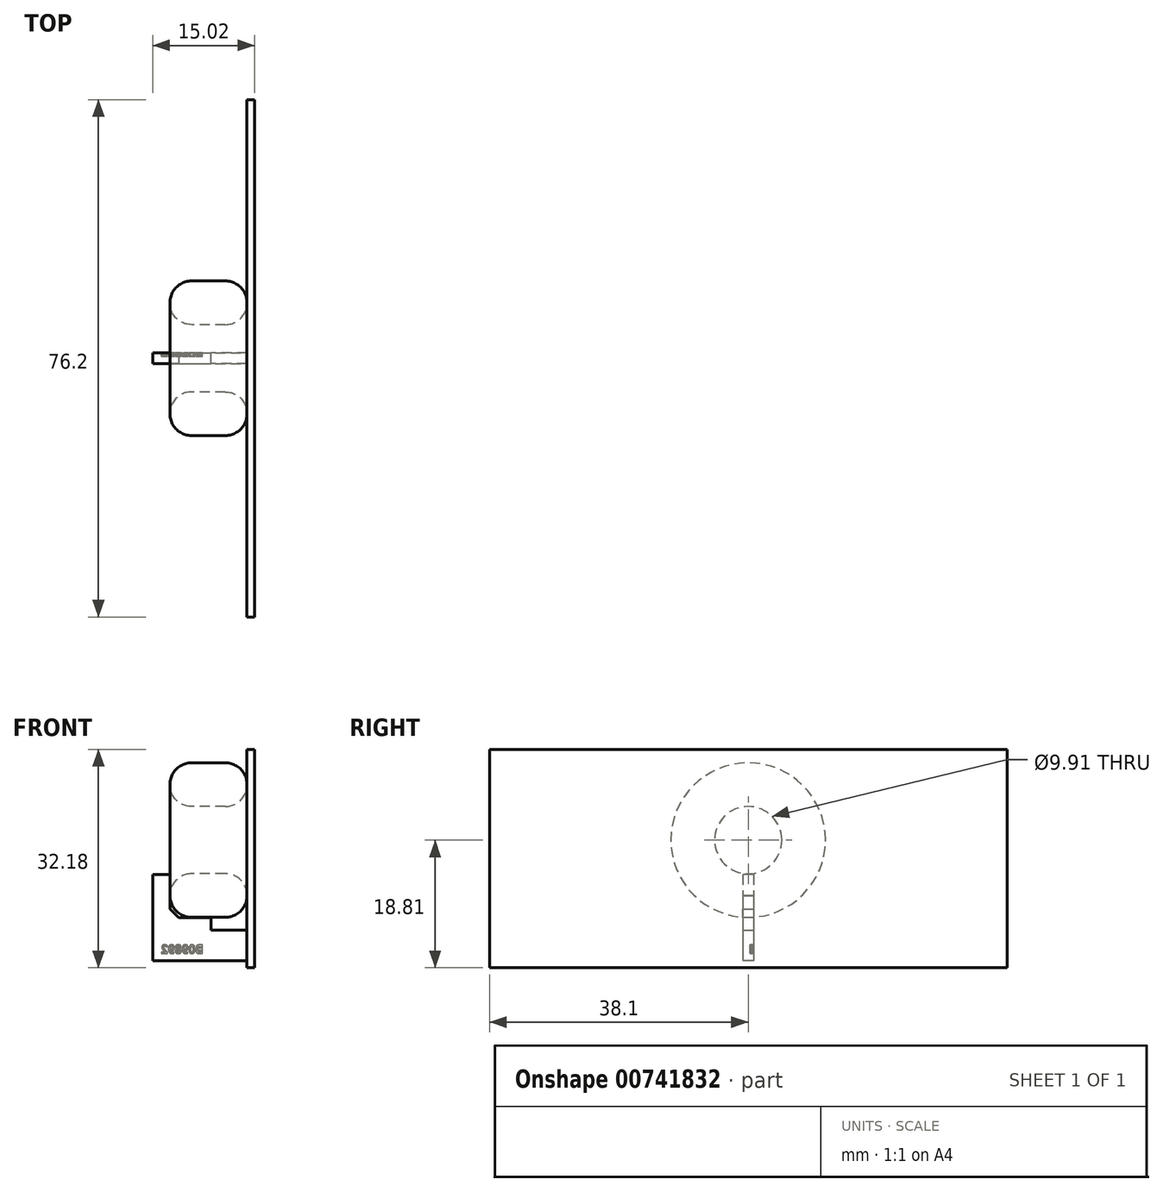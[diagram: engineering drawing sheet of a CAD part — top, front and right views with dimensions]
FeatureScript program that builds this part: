
annotation { "Feature Type Name" : "Feature", "Feature Type Description" : "" }
export const myFeature = defineFeature(function(context is Context, id is Id, definition is map)
    precondition{}
    {
        {
            var Q0;
            Q0=qCreatedBy(makeId("Front.planeOp"),FACE);
            var sketch = newSketch(context, id + "F0", { "sketchPlane" : qUnion([Q0])});
            skLineSegment(sketch, "E0.bottom", {"start": v(-11.35, 11.38) * mm, "end": v(0, 11.38) * mm});
            skLineSegment(sketch, "E0.top", {"start": v(-11.35, 4.95) * mm, "end": v(0, 4.95) * mm});
            skLineSegment(sketch, "E0.left", {"start": v(-11.35, 11.38) * mm, "end": v(-11.35, 4.95) * mm});
            skLineSegment(sketch, "E0.right", {"start": v(0, 11.38) * mm, "end": v(0, 4.95) * mm});
            skLineSegment(sketch, "E1", {"start": v(-10.58, 0) * mm, "end": v(-3.24, 0) * mm, "construction": true});
            skLineSegment(sketch, "E2.bottom", {"start": v(0, 13.37) * mm, "end": v(1.13, 13.37) * mm});
            skLineSegment(sketch, "E2.top", {"start": v(0, -18.8) * mm, "end": v(1.13, -18.8) * mm});
            skLineSegment(sketch, "E2.left", {"start": v(0, 13.37) * mm, "end": v(0, -18.8) * mm});
            skLineSegment(sketch, "E2.right", {"start": v(1.13, 13.37) * mm, "end": v(1.13, -18.8) * mm});
            skLineSegment(sketch, "E3.bottom", {"start": v(1.13, 13.37) * mm, "end": v(1.13, 13.37) * mm});
            skSolve(sketch);
        }
        {
            var Q0;
            Q0=makeQuery(id+"F0.imprint","IMPRINT",FACE,{"disambiguationData":[TD([[makeQuery(id+"F0.imprint","IMPRINT",EDGE,{"derivedFrom":sQuery(id+"F0.wireOp",EDGE,"E0.bottom")}),-1.0]])]});
            var Q1;
            Q1=sQuery(id+"F0.wireOp",EDGE,"E1");
            revolve(context, id + "F1", {"surfaceOperationType" : NewSurfaceOperationType.NEW, "entities" : qUnion([Q0]), "axis" : qUnion([Q1]), "revolveType" : RevolveType.FULL});
        }
        {
            var Q0;
            Q0=makeQuery(id+"F1.opRevolve","SWEPT_EDGE",EDGE,{"disambiguationData":[OSD([sQuery(id+"F0.wireOp",EDGE,"E0.top"),sQuery(id+"F0.wireOp",EDGE,"E0.left")])]});
            var Q1;
            Q1=makeQuery(id+"F1.opRevolve","SWEPT_EDGE",EDGE,{"disambiguationData":[OSD([sQuery(id+"F0.wireOp",EDGE,"E0.bottom"),sQuery(id+"F0.wireOp",EDGE,"E0.left")])]});
            var Q2;
            Q2=makeQuery(id+"F1.opRevolve","SWEPT_FACE",FACE,{"disambiguationData":[OSD([sQuery(id+"F0.wireOp",EDGE,"E0.bottom")])]});
            var Q3;
            Q3=makeQuery(id+"F1.opRevolve","SWEPT_FACE",FACE,{"disambiguationData":[OSD([sQuery(id+"F0.wireOp",EDGE,"E0.right")])]});
            fillet(context, id + "F2", {"entities" : qUnion([Q0, Q1, Q2, Q3]), "radius" : 3.17 * mm, "tangentPropagation" : true, "allowEdgeOverflow" : false});
        }
        {
            var Q0;
            {var subQ3=sQuery(id+"F0.wireOp",EDGE,"E2.bottom");Q0=makeQuery(id+"F0.imprint","IMPRINT",FACE,{"disambiguationData":[TD([[makeQuery(id+"F0.imprint","IMPRINT",EDGE,{"derivedFrom":subQ3}),-1.0]])]});}
            extrude(context, id + "F3", {"entities" : qUnion([Q0]), "endBound" : BoundingType.SYMMETRIC, "depth" : 76.2 * mm, "offsetDistance" : 25.4 * mm});
        }
        {
            var Q0;
            Q0=qCreatedBy(makeId("Right.planeOp"),FACE);
            var sketch = newSketch(context, id + "F4", { "sketchPlane" : qUnion([Q0])});
            skLineSegment(sketch, "E4.bottom", {"start": v(0, -11.44) * mm, "end": v(-0.79, -11.44) * mm});
            skLineSegment(sketch, "E4.top", {"start": v(0.79, -17.8) * mm, "end": v(-0.79, -17.8) * mm});
            skLineSegment(sketch, "E4.left", {"start": v(0.79, -11.44) * mm, "end": v(0.79, -17.8) * mm});
            skLineSegment(sketch, "E4.right", {"start": v(-0.79, -11.44) * mm, "end": v(-0.79, -17.8) * mm});
            skLineSegment(sketch, "E5", {"start": v(0.79, -11.44) * mm, "end": v(0, -11.44) * mm});
            skSolve(sketch);
        }
        {
            var Q0;
            Q0=makeQuery(id+"F4.imprint","IMPRINT",FACE,{"disambiguationData":[TD([[makeQuery(id+"F4.imprint","IMPRINT",EDGE,{"derivedFrom":sQuery(id+"F4.wireOp",EDGE,"E4.bottom")}),1.0]])]});
            extrude(context, id + "F5", {"entities" : qUnion([Q0]), "oppositeDirection" : true, "depth" : 11.35 * mm, "offsetDistance" : 25.4 * mm});
        }
        {
            var Q0;
            Q0=makeQuery(id+"F5.opExtrude","SWEPT_FACE",FACE,{"disambiguationData":[OSD([sQuery(id+"F4.wireOp",EDGE,"E4.left")])]});
            var sketch = newSketch(context, id + "F6", { "sketchPlane" : qUnion([Q0])});
            skLineSegment(sketch, "E6.bottom", {"start": v(0, -11.44) * mm, "end": v(5.3, -11.44) * mm});
            skLineSegment(sketch, "E6.top", {"start": v(0, -13.3) * mm, "end": v(5.3, -13.3) * mm});
            skLineSegment(sketch, "E6.left", {"start": v(0, -11.44) * mm, "end": v(0, -13.3) * mm});
            skLineSegment(sketch, "E6.right", {"start": v(5.3, -11.44) * mm, "end": v(5.3, -13.3) * mm});
            skSolve(sketch);
        }
        {
            var Q0;
            Q0 = qSketchRegion(id + "F6", true);
            extrude(context, id + "F7", {"entities" : qUnion([Q0]), "operationType" : NewBodyOperationType.REMOVE, "endBound" : BoundingType.UP_TO_NEXT, "oppositeDirection" : true, "depth" : 25.4 * mm, "offsetDistance" : 25.4 * mm});
        }
        {
            var Q0;
            Q0=makeQuery(id+"F5.opExtrude","CAP_FACE",FACE,{"disambiguationData":[OSD([sQuery(id+"F4.wireOp",EDGE,"E4.bottom"),sQuery(id+"F4.wireOp",EDGE,"E4.top"),sQuery(id+"F4.wireOp",EDGE,"E4.left"),sQuery(id+"F4.wireOp",EDGE,"E4.right"),sQuery(id+"F4.wireOp",EDGE,"E5")])],"isStart":false});
            var sketch = newSketch(context, id + "F8", { "sketchPlane" : qUnion([Q0])});
            skPoint(sketch, "E7.oppositeSnap0", {"position": v(0.79, -14.62) * mm});
            skLineSegment(sketch, "E7.bottom", {"start": v(-0.79, -17.8) * mm, "end": v(0.79, -17.8) * mm});
            skLineSegment(sketch, "E7.top", {"start": v(-0.79, -5.1) * mm, "end": v(0.79, -5.1) * mm});
            skLineSegment(sketch, "E7.left", {"start": v(-0.79, -17.8) * mm, "end": v(-0.79, -5.1) * mm});
            skLineSegment(sketch, "E7.right", {"start": v(0.79, -17.8) * mm, "end": v(0.79, -5.1) * mm});
            skSolve(sketch);
        }
        {
            var Q0;
            Q0 = qSketchRegion(id + "F8", true);
            extrude(context, id + "F9", {"entities" : qUnion([Q0]), "operationType" : NewBodyOperationType.ADD, "depth" : 2.54 * mm, "offsetDistance" : 25.4 * mm});
        }
        {
            var Q0;
            Q0=makeQuery(id+"F5.opExtrude","CAP_EDGE",EDGE,{"disambiguationData":[OSD([sQuery(id+"F4.wireOp",EDGE,"E4.bottom"),sQuery(id+"F4.wireOp",EDGE,"E5")])],"isStart":false});
            chamfer(context, id + "F10", {"entities" : qUnion([Q0]), "width" : 1.27 * mm, "tangentPropagation" : true});
        }
        {
            var Q0;
            Q0=makeQuery(id+"F9.boolean.opBoolean","MERGE",FACE,{"derivedFrom":[makeQuery(id+"F5.opExtrude","SWEPT_FACE",FACE,{"disambiguationData":[OSD([sQuery(id+"F4.wireOp",EDGE,"E4.left")])]}),makeQuery(id+"F9.opExtrude","SWEPT_FACE",FACE,{"disambiguationData":[OSD([sQuery(id+"F8.wireOp",EDGE,"E7.left")])]})]});
            var sketch = newSketch(context, id + "F11", { "sketchPlane" : qUnion([Q0])});
            skText(sketch, "E8", { "text": "B09892", "fontName": "OpenSans-Bold.ttf"});
            const initialGuessF11  = {"E8": [0.00642, -0.0167, 1, 0, 0.00127]};
            skSetInitialGuess(sketch, initialGuessF11);
            skSolve(sketch);
        }
        {
            var Q0;
            Q0 = qSketchRegion(id + "F11", true);
            extrude(context, id + "F12", {"entities" : qUnion([Q0]), "operationType" : NewBodyOperationType.REMOVE, "oppositeDirection" : true, "depth" : 0.5 * mm, "offsetDistance" : 25.4 * mm});
        }
    });
